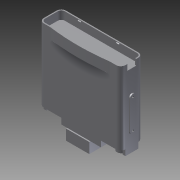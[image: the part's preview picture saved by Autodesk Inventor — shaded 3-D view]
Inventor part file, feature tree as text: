
AUTODESK INVENTOR PART (.ipt)
format: ipt  version: 2014 (Build 180170000, 170)  size: 366,592 bytes
history: native  units: mm
features: extrude x12, sketch x12, chamfer x4, hole x4, fillet x1
ambient origin geometry x8: Origin, YZ Plane, XZ Plane, XY Plane, X Axis, Y Axis, Z Axis, Center Point
bodies: Solid1 (feature_tree)
feature tree (33):
  extrude  "Extrusion1"  Depth=38.0mm
  extrude  "Extrusion2"  Depth=19.0mm
  extrude  "Extrusion3"  Depth=8.0mm
  extrude  "Extrusion4"  Depth=8.0mm
  chamfer  "Chamfer1"  Distance=18.0mm
  chamfer  "Chamfer3"  Distance=14.0mm
  chamfer  "Chamfer4"  Distance=14.0mm
  chamfer  "Chamfer5"  Distance=38.0mm
  extrude  "Extrusion5"  Depth=8.0mm
  extrude  "Extrusion8"  Depth=8.0mm
  extrude  "Extrusion10"  TaperAngle=0.0deg  [1 undecoded]
  fillet  "Fillet2"  [1 undecoded]
  extrude  "Extrusion11"  Depth=8.0mm
  extrude  "Extrusion12"  TaperAngle=0.0deg  [1 undecoded]
  extrude  "Extrusion13"  Depth=5.0mm
  extrude  "Extrusion14"  Depth=5.0mm
  extrude  "Extrusion15"  Depth=8.0mm
  hole  "Hole1"  [1 undecoded]
  hole  "Hole2"  [1 undecoded]
  hole  "Hole3"  [1 undecoded]
  hole  "Hole4"  [1 undecoded]
  sketch  "Sketch1"  dims[d0=140.0mm d1=38.0mm]
  sketch  "Sketch2"  dims[d2=70.0mm d3=19.0mm]
  sketch  "Sketch3"  dims[d4=8.0mm d5=8.0mm]
  sketch  "Sketch4"  dims[d6=8.0mm d7=8.0mm d8=18.0mm d9=0.0mm]
  sketch  "Sketch5"  dims[d10=2.0mm d11=14.0mm d12=0.0mm]
  sketch  "Sketch8"  dims[d13=6.915756mm]
  sketch  "Sketch11"  dims[d14=10.0mm]
  sketch  "Sketch12"  dims[d15=15.0mm]
  sketch  "Sketch13"  dims[d16=7.5mm d17=14.0mm d18=0.0mm]
  sketch  "Sketch14"  dims[d19=38.0mm]
  sketch  "Sketch15"  dims[d20=5.0mm]
  sketch  "Sketch16"  dims[d21=5.0mm d22=38.0mm d23=1.0mm d24=1.0mm d25=0.0mm d26=0.0mm d28=1.0mm d29=0.0mm d30=5.0mm d31=5.0mm d33=1.0mm d34=0.0mm d36=13.0mm d37=0.0mm d38=1.0mm d39=1.0mm d40=45.0deg d44=1.0mm d45=1.0mm d46=45.0deg d47=1.0mm d48=1.0mm d49=45.0deg d50=1.0mm d51=1.0mm d52=45.0deg d53=10.0mm d54=5.0mm d55=11.0mm d56=0.0mm d59=66.0mm d60=74.0mm d63=2.0mm d64=18.0mm d65=18.0mm d66=5.5mm d67=30.0mm d68=30.0mm d69=10.0mm d70=0.0mm d78=107.0mm d79=0.0mm d80=60.0mm d81=15.0mm d82=21.0mm d83=20.0mm d84=17.0mm d85=0.0mm d86=0.0mm d87=0.0mm d88=0.0mm d89=5.0mm d90=0.0mm d91=0.0mm d92=0.0mm d93=5.0mm d94=10.0mm d95=0.0mm d96=38.0mm d97=68.0mm d98=0.0mm d99=0.0mm d100=10.0mm d101=0.0mm d102=40.0mm d103=40.0mm d104=0.0mm d105=10.0mm d106=18.0mm d107=0.0mm d108=52.0mm d109=10.0mm d110=10.0mm d111=50.0mm d113=19.0mm d114=19.0mm d115=2.0mm d116=142.0mm d117=0.0mm d118=0.0mm d119=10.0mm d120=10.0mm d121=3.242mm d122=6.0mm d123=4.0mm d124=2.0mm d125=90.0deg d126=8.0mm d127=20.594885mm d128=10.0mm d129=10.0mm d130=3.242mm d131=6.0mm d132=4.0mm d133=2.0mm d134=90.0deg d135=8.0mm d136=20.594885mm d137=10.0mm d138=10.0mm d139=3.242mm d140=6.0mm d141=4.0mm d142=2.0mm d143=90.0deg d144=8.0mm d145=20.594885mm d146=10.0mm d147=10.0mm d148=3.242mm d149=6.0mm d150=4.0mm d151=2.0mm d152=90.0deg d153=8.0mm d154=20.594885mm]
note: 7 required parameter values undecoded (feature->parameter linkage not recoverable at this tier; creation-order binding heuristic only, values carry confidence <= 0.55)
